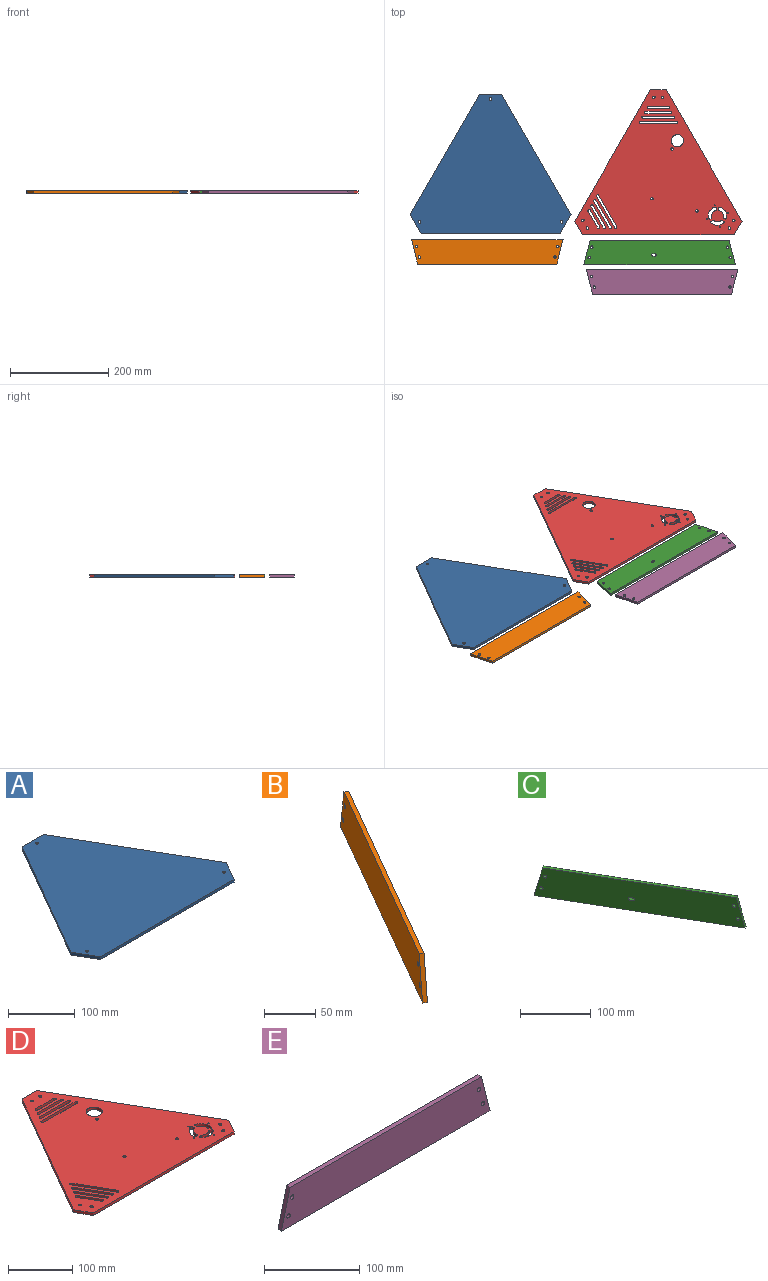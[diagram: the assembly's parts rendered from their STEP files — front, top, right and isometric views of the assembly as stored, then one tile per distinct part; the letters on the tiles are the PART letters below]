
ASSEMBLY  parts=5 mates=7
PART A: 11 faces, bbox 327.9x283.9x5 mm
  f0: plane 44.86x5mm, normal (0,1,0), area 224.3mm2, adj f1,f5,f6,f7
  f1: plane 245.1x141.51mm, normal (-0.87,0.5,0), area 1415.1mm2, adj f0,f2,f6,f7
  f2: plane 38.85x22.43mm, normal (-0.87,-0.5,0), area 224.3mm2, adj f1,f3,f6,f7
  f3: plane 283.02x5mm, normal (0,-1,0), area 1415.1mm2, adj f2,f4,f6,f7
  f4: plane 38.85x22.43mm, normal (0.87,-0.5,0), area 224.3mm2, adj f3,f5,f6,f7
  f5: plane 245.1x141.51mm, normal (0.87,0.5,0), area 1415.1mm2, adj f0,f4,f6,f7
  f6: plane 327.87x283.95mm, normal (0,0,-1), area 57484.9mm2, adj f0,f1,f2,f3,f4,f5,f8,f9
  f7: plane 327.87x283.95mm, normal (0,0,1), area 57484.9mm2, adj f0,f1,f2,f3,f4,f5,f8,f9
  f8: cylinder r=2.5mm len=5mm, axis (0,0,1), area 78.5mm2, adj f6,f7
  f9: cylinder r=2.5mm len=5mm, axis (0,0,1), area 78.5mm2, adj f6,f7
  f10: cylinder r=2.5mm len=5mm, axis (0,0,1), area 78.5mm2, adj f6,f7
PART B: 10 faces, bbox 158.6x269.7x50 mm
  f0: plane 247.6x145.84mm, normal (0,0,1), area 1415.1mm2, adj f1,f3,f4,f5
  f1: plane 50x13.55mm, normal (0.48,0.84,0.25), area 258mm2, adj f0,f2,f4,f5
  f2: plane 269.71x158.6mm, normal (0,0,-1), area 1542.7mm2, adj f1,f3,f4,f5
  f3: plane 50x13.55mm, normal (-0.48,-0.84,0.25), area 258mm2, adj f0,f2,f4,f5
  f4: plane 267.21x154.27mm, normal (0.87,-0.5,0), area 14710.5mm2, adj f0,f1,f2,f3,f6,f7,f8,f9
  f5: plane 267.21x154.27mm, normal (-0.87,0.5,0), area 14710.5mm2, adj f0,f1,f2,f3,f6,f7,f8,f9
  f6: cylinder r=2.5mm len=6.83mm, axis (-0.87,0.5,0), area 78.5mm2, adj f4,f5
  f7: cylinder r=2.5mm len=6.83mm, axis (-0.87,0.5,0), area 78.5mm2, adj f4,f5
  f8: cylinder r=2.5mm len=6.83mm, axis (-0.87,0.5,0), area 78.5mm2, adj f4,f5
  f9: cylinder r=2.5mm len=6.83mm, axis (-0.87,0.5,0), area 78.5mm2, adj f4,f5
PART C: 14 faces, bbox 158.6x269.7x50 mm
  f0: plane 247.6x145.84mm, normal (0,0,1), area 1415.1mm2, adj f1,f3,f4,f5
  f1: plane 50x13.55mm, normal (0.48,-0.84,0.25), area 258mm2, adj f0,f2,f4,f5
  f2: plane 269.71x158.6mm, normal (0,0,-1), area 1542.7mm2, adj f1,f3,f4,f5
  f3: plane 50x13.55mm, normal (-0.48,0.84,0.25), area 258mm2, adj f0,f2,f4,f5
  f4: plane 267.21x154.27mm, normal (-0.87,-0.5,0), area 14670.8mm2, adj f0,f1,f2,f3,f6,f7,f8,f9
  f5: plane 267.21x154.27mm, normal (0.87,0.5,0), area 14670.8mm2, adj f0,f1,f2,f3,f6,f7,f8,f9
  f6: cylinder r=2.5mm len=6.83mm, axis (0.87,0.5,0), area 78.5mm2, adj f4,f5
  f7: cylinder r=2.5mm len=6.83mm, axis (0.87,0.5,0), area 78.5mm2, adj f4,f5
  f8: cylinder r=2.5mm len=6.83mm, axis (0.87,0.5,0), area 78.5mm2, adj f4,f5
  f9: cylinder r=2.5mm len=6.83mm, axis (0.87,0.5,0), area 78.5mm2, adj f4,f5
  f10: plane 6.33x5.96mm, normal (0,0,-1), area 20mm2, adj f4,f5,f11,f13
  f11: cylinder r=2.5mm len=5.58mm, axis (0.87,0.5,0), area 39.3mm2, adj f4,f5,f10,f12
  f12: plane 6.33x5.96mm, normal (0,0,1), area 20mm2, adj f4,f5,f11,f13
  f13: cylinder r=2.5mm len=5.58mm, axis (0.87,0.5,0), area 39.3mm2, adj f4,f5,f10,f12
PART D: 78 faces, bbox 340.6x295x5 mm
  f0: plane 340.64x295mm, normal (0,0,-1), area 55189mm2, adj f2,f3,f4,f5,f6,f7,f8,f9
  f1: plane 340.64x295mm, normal (0,0,1), area 55189mm2, adj f2,f3,f4,f5,f6,f7,f8,f9
  f2: plane 32.09x5mm, normal (0,1,0), area 160.5mm2, adj f0,f1,f3,f7
  f3: plane 267.21x154.27mm, normal (-0.87,0.5,0), area 1542.7mm2, adj f0,f1,f2,f4
  f4: plane 27.79x16.05mm, normal (-0.87,-0.5,0), area 160.5mm2, adj f0,f1,f3,f5
  f5: plane 308.54x5mm, normal (0,-1,0), area 1542.7mm2, adj f0,f1,f4,f6
  f6: plane 27.79x16.05mm, normal (0.87,-0.5,0), area 160.5mm2, adj f0,f1,f5,f7
  f7: plane 267.21x154.27mm, normal (0.87,0.5,0), area 1542.7mm2, adj f0,f1,f2,f6
  f8: cylinder r=1mm len=5mm, axis (0,0,1), area 31.4mm2, adj f0,f1
  f9: cylinder r=1mm len=5mm, axis (0,0,1), area 31.4mm2, adj f0,f1
  f10: cylinder r=1mm len=5mm, axis (0,0,1), area 31.4mm2, adj f0,f1
  f11: cylinder r=1mm len=5mm, axis (0,0,1), area 31.4mm2, adj f0,f1
  f12: cylinder r=2.5mm len=5mm, axis (0,0,1), area 78.5mm2, adj f0,f1
  f13: cylinder r=2.5mm len=5mm, axis (0,0,1), area 78.5mm2, adj f0,f1
  f14: cylinder r=2.5mm len=5mm, axis (0,0,1), area 78.5mm2, adj f0,f1
  f15: cylinder r=12mm len=13.7mm, axis (0,0,1), area 86.4mm2, adj f0,f1,f35,f38
  f16: plane 5x2.88mm, normal (-1,0,0), area 14.4mm2, adj f0,f1,f37,f38
  f17: cylinder r=18.75mm len=22.73mm, axis (0,0,1), area 145.3mm2, adj f0,f1,f36,f37
  f18: plane 5x2.49mm, normal (-0.5,0.87,0), area 14.4mm2, adj f0,f1,f35,f36
  f19: plane 5x2.49mm, normal (0.5,0.87,0), area 14.4mm2, adj f0,f1,f31,f34
  f20: cylinder r=18.75mm len=22.73mm, axis (0,0,1), area 145.3mm2, adj f0,f1,f31,f32
  f21: plane 5x2.88mm, normal (1,0,0), area 14.4mm2, adj f0,f1,f32,f33
  f22: cylinder r=12mm len=13.7mm, axis (0,0,1), area 86.4mm2, adj f0,f1,f33,f34
  f23: cylinder r=12mm len=15.82mm, axis (0,0,1), area 86.4mm2, adj f0,f1,f27,f30
  f24: plane 5x2.49mm, normal (0.5,-0.87,0), area 14.4mm2, adj f0,f1,f29,f30
  f25: cylinder r=18.75mm len=26.24mm, axis (0,0,1), area 145.3mm2, adj f0,f1,f28,f29
  f26: plane 5x2.49mm, normal (-0.5,-0.87,0), area 14.4mm2, adj f0,f1,f27,f28
  f27: cylinder r=2mm len=5mm, axis (0,0,1), area 12.4mm2, adj f0,f1,f23,f26
  f28: cylinder r=2mm len=5mm, axis (0,0,1), area 18.4mm2, adj f0,f1,f25,f26
  f29: cylinder r=2mm len=5mm, axis (0,0,1), area 18.4mm2, adj f0,f1,f24,f25
  f30: cylinder r=2mm len=5mm, axis (0,0,1), area 12.4mm2, adj f0,f1,f23,f24
  f31: cylinder r=2mm len=5mm, axis (0,0,1), area 18.4mm2, adj f0,f1,f19,f20
  f32: cylinder r=2mm len=5mm, axis (0,0,1), area 18.4mm2, adj f0,f1,f20,f21
  f33: cylinder r=2mm len=5mm, axis (0,0,1), area 12.4mm2, adj f0,f1,f21,f22
  f34: cylinder r=2mm len=5mm, axis (0,0,1), area 12.4mm2, adj f0,f1,f19,f22
  f35: cylinder r=2mm len=5mm, axis (0,0,1), area 12.4mm2, adj f0,f1,f15,f18
  f36: cylinder r=2mm len=5mm, axis (0,0,1), area 18.4mm2, adj f0,f1,f17,f18
  f37: cylinder r=2mm len=5mm, axis (0,0,1), area 18.4mm2, adj f0,f1,f16,f17
  f38: cylinder r=2mm len=5mm, axis (0,0,1), area 12.4mm2, adj f0,f1,f15,f16
  f39: plane 50.58x5mm, normal (0,-1,0), area 252.9mm2, adj f0,f1,f40,f42
  f40: cylinder r=2.5mm len=5mm, axis (0,0,1), area 39.3mm2, adj f0,f1,f39,f41
  f41: plane 50.58x5mm, normal (0,1,0), area 252.9mm2, adj f0,f1,f40,f42
  f42: cylinder r=2.5mm len=5mm, axis (0,0,1), area 39.3mm2, adj f0,f1,f39,f41
  f43: plane 62.13x5mm, normal (0,-1,0), area 310.6mm2, adj f0,f1,f44,f46
  f44: cylinder r=2.5mm len=5mm, axis (0,0,1), area 39.3mm2, adj f0,f1,f43,f45
  f45: plane 62.13x5mm, normal (0,1,0), area 310.6mm2, adj f0,f1,f44,f46
  f46: cylinder r=2.5mm len=5mm, axis (0,0,1), area 39.3mm2, adj f0,f1,f43,f45
  f47: plane 73.67x5mm, normal (0,1,0), area 368.4mm2, adj f0,f1,f48,f50
  f48: cylinder r=2.5mm len=5mm, axis (0,0,1), area 39.3mm2, adj f0,f1,f47,f49
  f49: plane 73.67x5mm, normal (0,-1,0), area 368.4mm2, adj f0,f1,f48,f50
  f50: cylinder r=2.5mm len=5mm, axis (0,0,1), area 39.3mm2, adj f0,f1,f47,f49
  f51: cylinder r=2.5mm len=5mm, axis (0,0,1), area 39.3mm2, adj f0,f1,f52,f54
  f52: plane 53.8x31.06mm, normal (0.87,0.5,0), area 310.6mm2, adj f0,f1,f51,f53
  f53: cylinder r=2.5mm len=5mm, axis (0,0,1), area 39.3mm2, adj f0,f1,f52,f54
  f54: plane 53.8x31.06mm, normal (-0.87,-0.5,0), area 310.6mm2, adj f0,f1,f51,f53
  f55: cylinder r=2.5mm len=5mm, axis (0,0,1), area 39.3mm2, adj f0,f1,f56,f58
  f56: plane 63.8x36.84mm, normal (-0.87,-0.5,0), area 368.4mm2, adj f0,f1,f55,f57
  f57: cylinder r=2.5mm len=5mm, axis (0,0,1), area 39.3mm2, adj f0,f1,f56,f58
  f58: plane 63.8x36.84mm, normal (0.87,0.5,0), area 368.4mm2, adj f0,f1,f55,f57
  f59: cylinder r=2.5mm len=5mm, axis (0,0,1), area 39.3mm2, adj f0,f1,f60,f62
  f60: plane 43.8x25.29mm, normal (0.87,0.5,0), area 252.9mm2, adj f0,f1,f59,f61
  f61: cylinder r=2.5mm len=5mm, axis (0,0,1), area 39.3mm2, adj f0,f1,f60,f62
  f62: plane 43.8x25.29mm, normal (-0.87,-0.5,0), area 252.9mm2, adj f0,f1,f59,f61
  f63: cylinder r=2.5mm len=5mm, axis (0,0,1), area 39.3mm2, adj f0,f1,f64,f66
  f64: plane 33.8x19.52mm, normal (-0.87,-0.5,0), area 195.2mm2, adj f0,f1,f63,f65
  f65: cylinder r=2.5mm len=5mm, axis (0,0,1), area 39.3mm2, adj f0,f1,f64,f66
  f66: plane 33.8x19.52mm, normal (0.87,0.5,0), area 195.2mm2, adj f0,f1,f63,f65
  f67: plane 39.03x5mm, normal (0,-1,0), area 195.2mm2, adj f0,f1,f68,f70
  f68: cylinder r=2.5mm len=5mm, axis (0,0,1), area 39.3mm2, adj f0,f1,f67,f69
  f69: plane 39.03x5mm, normal (0,1,0), area 195.2mm2, adj f0,f1,f68,f70
  f70: cylinder r=2.5mm len=5mm, axis (0,0,1), area 39.3mm2, adj f0,f1,f67,f69
  f71: cylinder r=12.5mm len=25mm, axis (0,0,1), area 392.7mm2, adj f0,f1
  f72: cylinder r=2.5mm len=5mm, axis (0,0,-1), area 78.5mm2, adj f0,f1
  f73: cylinder r=2.5mm len=5mm, axis (0,0,-1), area 78.5mm2, adj f0,f1
  f74: cylinder r=2.5mm len=5mm, axis (0,0,-1), area 78.5mm2, adj f0,f1
  f75: cylinder r=2.5mm len=5mm, axis (0,0,-1), area 78.5mm2, adj f0,f1
  f76: cylinder r=2.5mm len=5mm, axis (0,0,-1), area 78.5mm2, adj f0,f1
  f77: cylinder r=2.5mm len=5mm, axis (0,0,-1), area 78.5mm2, adj f0,f1
PART E: 10 faces, bbox 308.5x5x50 mm
  f0: plane 283.02x5mm, normal (0,0,1), area 1415.1mm2, adj f1,f3,f4,f5
  f1: plane 50x12.76mm, normal (-0.97,0,0.25), area 258mm2, adj f0,f2,f4,f5
  f2: plane 308.54x5mm, normal (0,0,-1), area 1542.7mm2, adj f1,f3,f4,f5
  f3: plane 50x12.76mm, normal (0.97,0,0.25), area 258mm2, adj f0,f2,f4,f5
  f4: plane 308.54x50mm, normal (0,1,0), area 14710.5mm2, adj f0,f1,f2,f3,f6,f7,f8,f9
  f5: plane 308.54x50mm, normal (0,-1,0), area 14710.5mm2, adj f0,f1,f2,f3,f6,f7,f8,f9
  f6: cylinder r=2.5mm len=5mm, axis (0,-1,0), area 78.5mm2, adj f4,f5
  f7: cylinder r=2.5mm len=5mm, axis (0,-1,0), area 78.5mm2, adj f4,f5
  f8: cylinder r=2.5mm len=5mm, axis (0,-1,0), area 78.5mm2, adj f4,f5
  f9: cylinder r=2.5mm len=5mm, axis (0,-1,0), area 78.5mm2, adj f4,f5
PLACE A t=(-353.2,-4.94,0)mm fixed
PLACE B rot(axis=(0.38,-0.65,0.65),138.6deg) t=(-359.85,-896.36,-614.58)mm
PLACE C rot(axis=(-0.77,0.45,0.45),104.5deg) t=(-8.9,596.78,-614.58)mm
PLACE D t=(-11.49,-6.87,55)mm
PLACE E rot(axis=(1,0,0),90deg) t=(-3.85,-957.55,-614.58)mm
MATE planar D.f1 <-> A.f7  axis (0,0,1) through (-10.54,-8.37,-717.17)mm
MATE parallel C.f2 <-> B.f2  axis (0,-1,0) through (-8.9,-175.39,-719.67)mm
MATE parallel E.f0 <-> C.f0  axis (0,-1,0) through (-3.85,-235.37,-719.67)mm
MATE planar C.f4 <-> E.f4  axis (0,0,1) through (-8.87,-150.74,-717.17)mm
MATE planar B.f4 <-> A.f7  axis (0,0,1) through (-359.85,-148.82,-717.17)mm
MATE planar C.f4 <-> B.f4  axis (0,0,1) through (-8.87,-150.74,-717.17)mm
MATE parallel B.f0 <-> A.f3  axis (0,-1,0) through (-359.85,-174.18,-719.67)mm
